# Revit family: Тактильная плитка (высокопрочный бетон, армированный фиброй) конус линейный
name_source: partatom
category: Оборудование
revit_build: Autodesk Revit 2017 (Build: 20160225_1515(x64)
units: mm (PartAtom-declared; Revit-internal decimal feet)

## family parameters
Общий = Да
Основа = Грань
При загрузке вырезать с полостями = Да
Размер круглого соединителя = Использовать диаметр
Тип детали = Нормальный
Точка расчета площади = Нет

## types (1)
- Тактильная плитка (высокопрочный бетон, армированный фиброй) конус линейный.
    ADSK_Код изделия = 10252-ZH
    ADSK_Материал наименование = Высокопрочный бетон армированный фиброй, цвет желтый
    ADSK_Материал плитки = Высокопрочный бетон армированный фиброй_Желтый
    ADSK_Наименование = Тактильная плитка (высокопрочный бетон, армированный фиброй) конус линейный.
    ADSK_Размер_Высота рифа = 5 мм
    ADSK_Размер_Габариты = 300x300x30мм
    ADSK_Размер_Длина = 300 мм
    ADSK_Размер_Толщина = 30 мм
    ADSK_Размер_Ширина = 300 мм
    ADSK_Тип рифов = Конусообразные рифы в линейном порядке
    URL = http://tiflocentre.ru
    Изготовитель = ТИФЛОЦЕНТР «ВЕРТИКАЛЬ»
    Описание = Тактильная желтая плитка состоит из высокопрочного бетона, армированный фиброй и предназначена для информирования при движении, как для тотально слепого человека, так и для слабовидящего человека. Расположение конусообразных рифов в линейном порядке позволяет использовать плитку для получения информации о преодолимых препятствиях. Тактильная бетонная плитка протестирована незрячими специалистами и рекомендована к применению ВОС и гос. программой "Доступная среда".
    Отметка по умолчанию = 0 мм
    Применение = Улица
    Стоимость = 88 $
